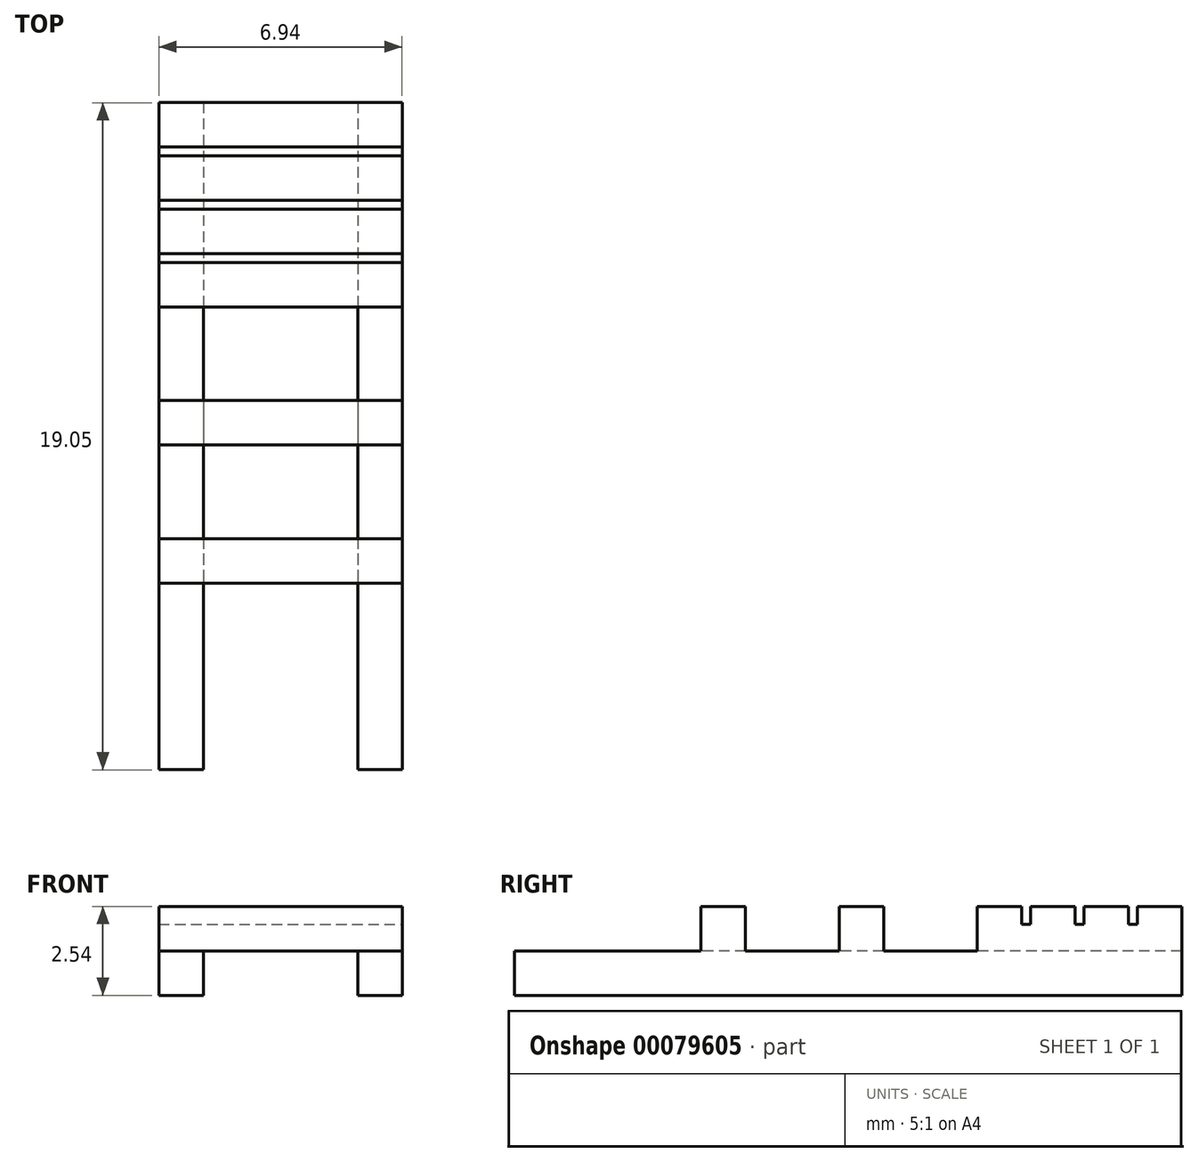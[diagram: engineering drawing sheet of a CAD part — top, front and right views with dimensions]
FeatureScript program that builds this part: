
annotation { "Feature Type Name" : "Feature", "Feature Type Description" : "" }
export const myFeature = defineFeature(function(context is Context, id is Id, definition is map)
    precondition{}
    {
        {
            var Q0;
            Q0=qCreatedBy(makeId("Top.planeOp"),FACE);
            var sketch = newSketch(context, id + "F0", { "sketchPlane" : qUnion([Q0])});
            skLineSegment(sketch, "E0.bottom", {"start": v(-3.47, 6.63) * mm, "end": v(-2.2, 6.63) * mm});
            skLineSegment(sketch, "E0.top", {"start": v(-3.47, -12.42) * mm, "end": v(-2.2, -12.42) * mm});
            skLineSegment(sketch, "E0.left", {"start": v(-3.47, 6.63) * mm, "end": v(-3.47, -12.42) * mm});
            skLineSegment(sketch, "E0.right", {"start": v(-2.2, 6.63) * mm, "end": v(-2.2, -12.42) * mm});
            skLineSegment(sketch, "E1.MirrorCS", {"start": v(3.47, 6.63) * mm, "end": v(2.2, 6.63) * mm});
            skLineSegment(sketch, "E2.MirrorCS", {"start": v(3.47, -12.42) * mm, "end": v(2.2, -12.42) * mm});
            skLineSegment(sketch, "E3.MirrorCS", {"start": v(3.47, 6.63) * mm, "end": v(3.47, -12.42) * mm});
            skLineSegment(sketch, "E4.MirrorCS", {"start": v(2.2, 6.63) * mm, "end": v(2.2, -12.42) * mm});
            skSolve(sketch);
        }
        {
            var Q0;
            Q0 = qSketchRegion(id + "F0", true);
            extrude(context, id + "F1", {"entities" : qUnion([Q0]), "depth" : 1.27 * mm});
        }
        {
            var Q0;
            Q0=makeQuery(id+"F1.opExtrude","CAP_FACE",FACE,{"disambiguationData":[OSD([sQuery(id+"F0.wireOp",EDGE,"E0.bottom"),sQuery(id+"F0.wireOp",EDGE,"E0.top"),sQuery(id+"F0.wireOp",EDGE,"E0.left"),sQuery(id+"F0.wireOp",EDGE,"E0.right")])],"isStart":false});
            var sketch = newSketch(context, id + "F2", { "sketchPlane" : qUnion([Q0])});
            skLineSegment(sketch, "E5.bottom", {"start": v(-3.47, 6.63) * mm, "end": v(3.47, 6.63) * mm});
            skLineSegment(sketch, "E5.top", {"start": v(-3.47, 5.36) * mm, "end": v(3.47, 5.36) * mm});
            skLineSegment(sketch, "E5.left", {"start": v(-3.47, 6.63) * mm, "end": v(-3.47, 5.36) * mm});
            skLineSegment(sketch, "E5.right", {"start": v(3.47, 6.63) * mm, "end": v(3.47, 5.36) * mm});
            skLineSegment(sketch, "E6.1.0.0", {"start": v(3.47, 5.1) * mm, "end": v(3.47, 3.84) * mm});
            skLineSegment(sketch, "E6.1.0.1", {"start": v(-3.47, 5.1) * mm, "end": v(-3.47, 3.84) * mm});
            skLineSegment(sketch, "E6.1.0.2", {"start": v(-3.47, 3.84) * mm, "end": v(3.47, 3.84) * mm});
            skLineSegment(sketch, "E6.1.0.3", {"start": v(-3.47, 5.1) * mm, "end": v(3.47, 5.1) * mm});
            skLineSegment(sketch, "E6.2.0.0", {"start": v(3.47, 3.59) * mm, "end": v(3.47, 2.32) * mm});
            skLineSegment(sketch, "E6.2.0.1", {"start": v(-3.47, 3.59) * mm, "end": v(-3.47, 2.32) * mm});
            skLineSegment(sketch, "E6.2.0.2", {"start": v(-3.47, 2.32) * mm, "end": v(3.47, 2.32) * mm});
            skLineSegment(sketch, "E6.2.0.3", {"start": v(-3.47, 3.59) * mm, "end": v(3.47, 3.59) * mm});
            skLineSegment(sketch, "E6.3.0.0", {"start": v(3.47, 2.06) * mm, "end": v(3.47, 0.8) * mm});
            skLineSegment(sketch, "E6.3.0.1", {"start": v(-3.47, 2.06) * mm, "end": v(-3.47, 0.8) * mm});
            skLineSegment(sketch, "E6.3.0.2", {"start": v(-3.47, 0.8) * mm, "end": v(3.47, 0.8) * mm});
            skLineSegment(sketch, "E6.3.0.3", {"start": v(-3.47, 2.06) * mm, "end": v(3.47, 2.06) * mm});
            skLineSegment(sketch, "E6.direction1", {"start": v(3.47, 5.36) * mm, "end": v(3.47, 3.84) * mm, "construction": true});
            skLineSegment(sketch, "E7.1.0.0", {"start": v(3.47, -1.88) * mm, "end": v(3.47, -3.15) * mm});
            skLineSegment(sketch, "E7.1.0.1", {"start": v(-3.47, -3.15) * mm, "end": v(3.47, -3.15) * mm});
            skLineSegment(sketch, "E7.1.0.2", {"start": v(-3.47, -1.88) * mm, "end": v(3.47, -1.88) * mm});
            skLineSegment(sketch, "E7.1.0.3", {"start": v(-3.47, -1.88) * mm, "end": v(-3.47, -3.15) * mm});
            skLineSegment(sketch, "E7.2.0.0", {"start": v(3.47, -5.82) * mm, "end": v(3.47, -7.09) * mm});
            skLineSegment(sketch, "E7.2.0.1", {"start": v(-3.47, -7.09) * mm, "end": v(3.47, -7.09) * mm});
            skLineSegment(sketch, "E7.2.0.2", {"start": v(-3.47, -5.82) * mm, "end": v(3.47, -5.82) * mm});
            skLineSegment(sketch, "E7.2.0.3", {"start": v(-3.47, -5.82) * mm, "end": v(-3.47, -7.09) * mm});
            skLineSegment(sketch, "E7.direction1", {"start": v(3.47, 0.8) * mm, "end": v(3.47, -3.15) * mm, "construction": true});
            skSolve(sketch);
        }
        {
            var Q0;
            Q0 = qSketchRegion(id + "F2", true);
            extrude(context, id + "F3", {"entities" : qUnion([Q0]), "operationType" : NewBodyOperationType.ADD, "depth" : 1.27 * mm});
        }
        {
            var Q0;
            {var subQ0=sQuery(id+"F2.wireOp",EDGE,"E6.3.0.2");var subQ2=sQuery(id+"F0.wireOp",EDGE,"E0.right");var subQ3=sQuery(id+"F0.wireOp",EDGE,"E0.left");Q0=makeQuery(id+"F3.boolean.opBoolean","SPLIT",FACE,{"disambiguationData":[TD([makeQuery(id+"F3.opExtrude","SWEPT_FACE",FACE,{"disambiguationData":[OSD([subQ0])]})])],"derivedFrom":makeQuery(id+"F1.opExtrude","CAP_FACE",FACE,{"disambiguationData":[OSD([sQuery(id+"F0.wireOp",EDGE,"E0.bottom"),sQuery(id+"F0.wireOp",EDGE,"E0.top"),subQ3,subQ2])],"isStart":false})});}
            var sketch = newSketch(context, id + "F4", { "sketchPlane" : qUnion([Q0])});
            skLineSegment(sketch, "E8.bottom", {"start": v(-3.47, 0.8) * mm, "end": v(3.47, 0.8) * mm});
            skLineSegment(sketch, "E8.top", {"start": v(-3.47, 6.63) * mm, "end": v(3.47, 6.63) * mm});
            skLineSegment(sketch, "E8.left", {"start": v(-3.47, 0.8) * mm, "end": v(-3.47, 6.63) * mm});
            skLineSegment(sketch, "E8.right", {"start": v(3.47, 0.8) * mm, "end": v(3.47, 6.63) * mm});
            skSolve(sketch);
        }
        {
            var Q0;
            Q0 = qSketchRegion(id + "F4", true);
            extrude(context, id + "F5", {"entities" : qUnion([Q0]), "operationType" : NewBodyOperationType.ADD, "depth" : 0.76 * mm});
        }
    });
